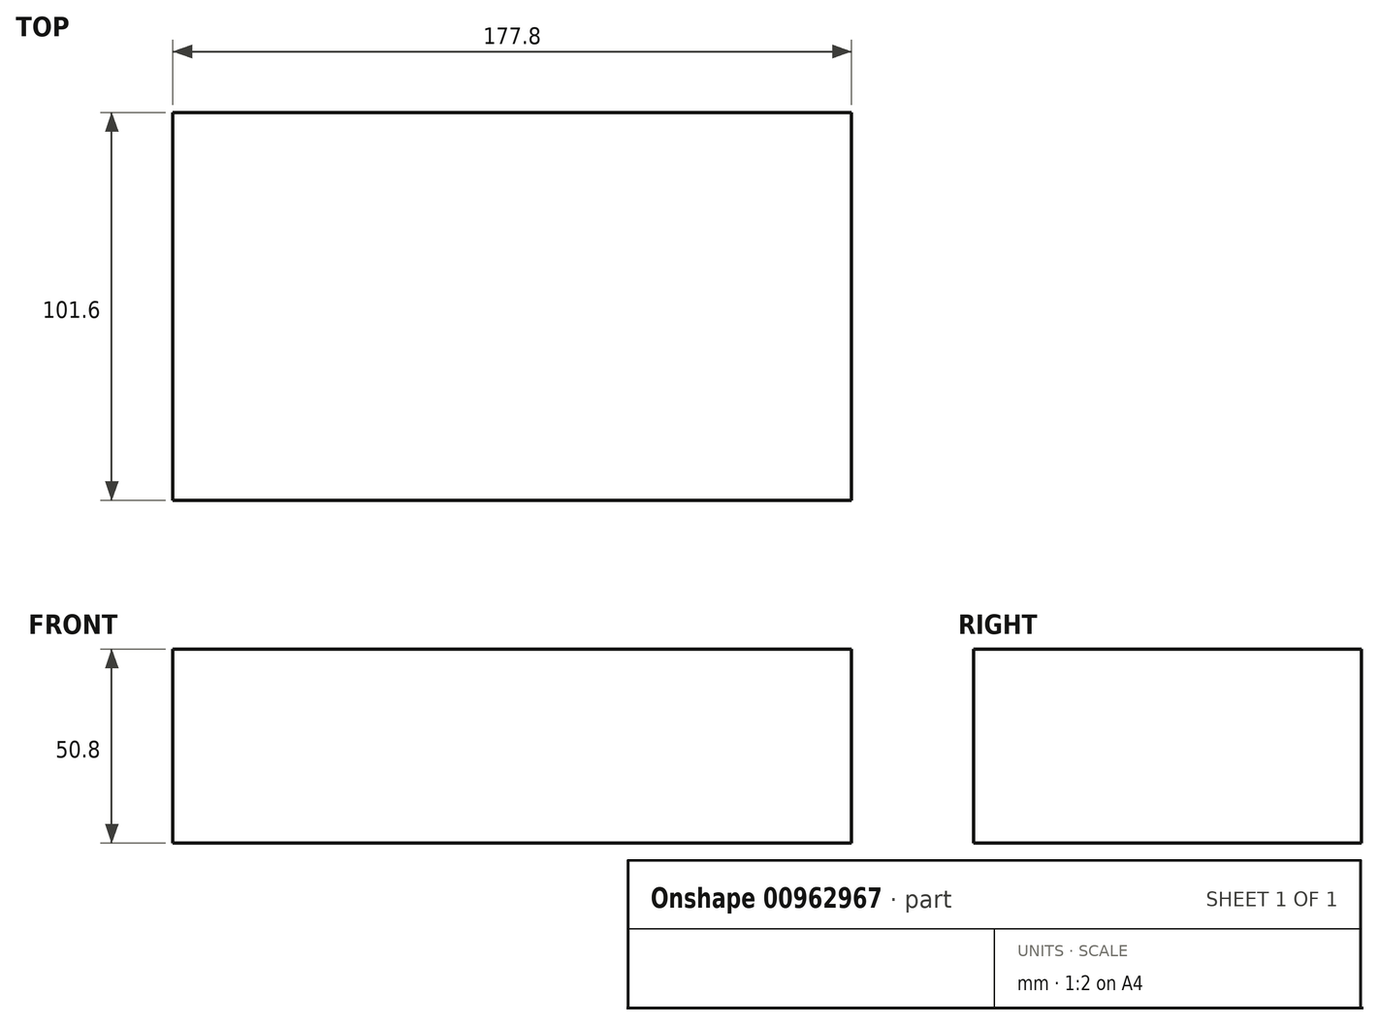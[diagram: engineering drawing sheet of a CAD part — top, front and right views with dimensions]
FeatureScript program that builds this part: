
annotation { "Feature Type Name" : "Feature", "Feature Type Description" : "" }
export const myFeature = defineFeature(function(context is Context, id is Id, definition is map)
    precondition{}
    {
        {
            var Q0;
            Q0=qCreatedBy(makeId("Top.planeOp"),FACE);
            var sketch = newSketch(context, id + "F0", { "sketchPlane" : qUnion([Q0])});
            skLineSegment(sketch, "E0.bottom", {"start": v(-87.44, 42.87) * mm, "end": v(90.36, 42.87) * mm});
            skLineSegment(sketch, "E0.top", {"start": v(-87.44, -58.73) * mm, "end": v(90.36, -58.73) * mm});
            skLineSegment(sketch, "E0.left", {"start": v(-87.44, 42.87) * mm, "end": v(-87.44, -58.73) * mm});
            skLineSegment(sketch, "E0.right", {"start": v(90.36, 42.87) * mm, "end": v(90.36, -58.73) * mm});
            skSolve(sketch);
        }
        {
            var Q0;
            Q0=makeQuery(id+"F0.imprint","IMPRINT",FACE,{"disambiguationData":[TD([[makeQuery(id+"F0.imprint","IMPRINT",EDGE,{"derivedFrom":sQuery(id+"F0.wireOp",EDGE,"E0.bottom")}),-1.0]])]});
            extrude(context, id + "F1", {"entities" : qUnion([Q0]), "depth" : 50.8 * mm, "offsetDistance" : 25.4 * mm});
        }
    });
